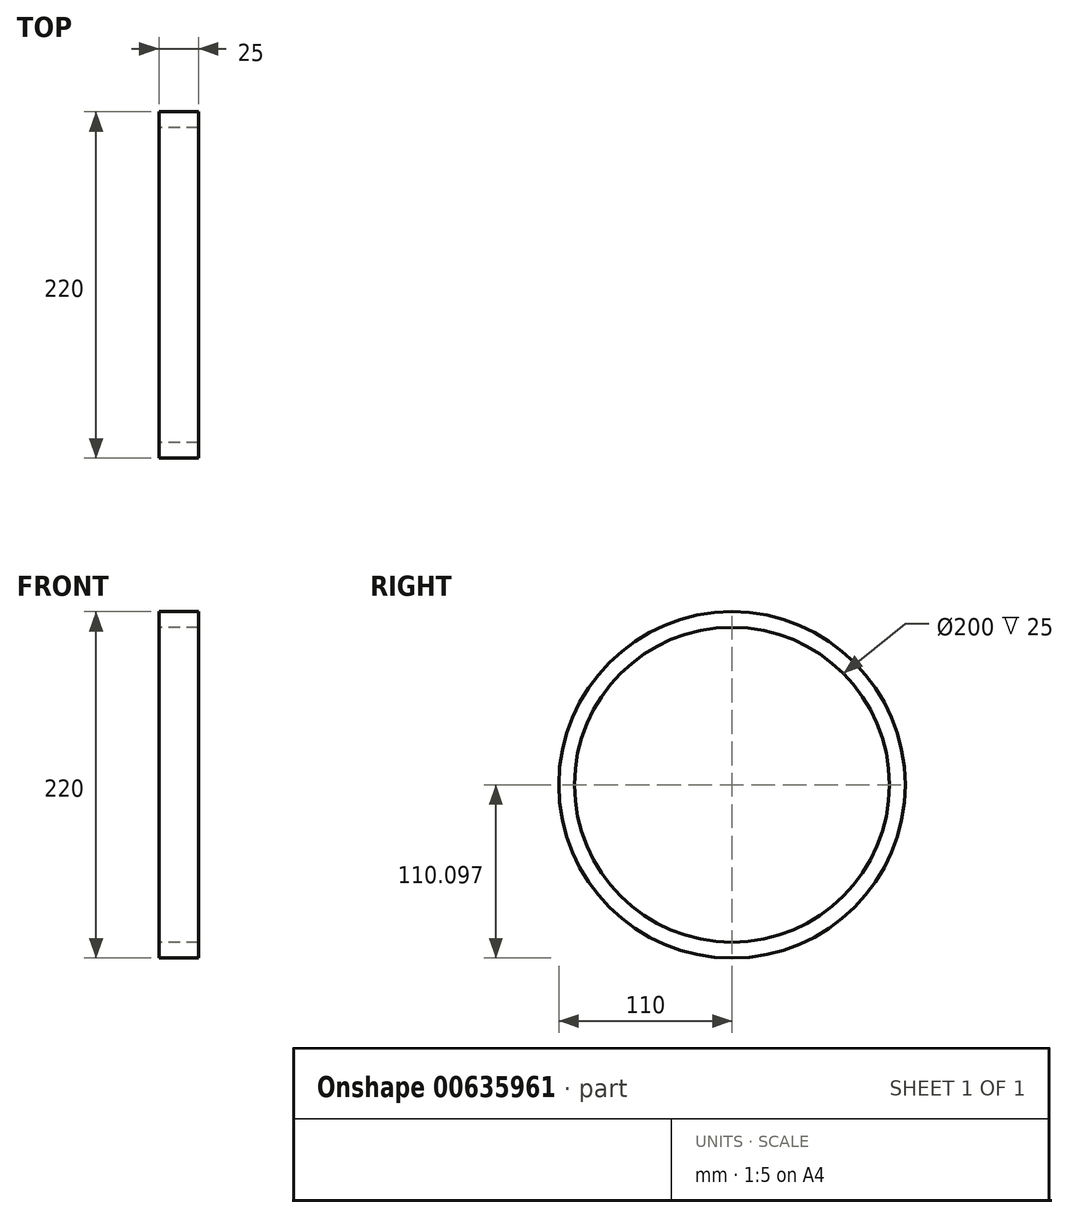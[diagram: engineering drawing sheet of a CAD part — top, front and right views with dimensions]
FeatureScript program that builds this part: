
annotation { "Feature Type Name" : "Feature", "Feature Type Description" : "" }
export const myFeature = defineFeature(function(context is Context, id is Id, definition is map)
    precondition{}
    {
        {
            var Q0;
            Q0=qCreatedBy(makeId("Right.planeOp"),FACE);
            var sketch = newSketch(context, id + "F0", { "sketchPlane" : qUnion([Q0])});
            skCircle(sketch, "E0", {"center": v(0, 0) * mm, "radius": 110 * mm});
            skCircle(sketch, "E1", {"center": v(0, 0.1) * mm, "radius": 100 * mm});
            skSolve(sketch);
        }
        {
            var Q0;
            Q0=makeQuery(id+"F0.imprint","IMPRINT",FACE,{"disambiguationData":[TD([[makeQuery(id+"F0.imprint","IMPRINT",EDGE,{"derivedFrom":sQuery(id+"F0.wireOp",EDGE,"E0")}),1.0]])]});
            extrude(context, id + "F1", {"entities" : qUnion([Q0]), "depth" : 25 * mm, "offsetDistance" : 25 * mm});
        }
    });
